# Revit family: IS_ConnectSpace_E1332_BIM_FR
name_source: partatom
category: Plumbing Fixtures
revit_build: Autodesk Revit 2017 (Build: 20160225_1515(x64)
units: mm (PartAtom-declared; Revit-internal decimal feet)

## family parameters
Always vertical = No
Cut with Voids When Loaded = No
OmniClass Number = 23.45.05.14.14
OmniClass Title = Sinks/Lavatories
Part Type = Normal
Room Calculation Point = No
Round Connector Dimension = Use Diameter
Shared = No
Work Plane-Based = No

## types (1)
- E1332 - Lavabo 55 x 38 cm
    Accessoires = www.idealstandard.be
    Assembly Code = C1030200
    Auteur = Ideal Standard
    BOSUseNativeGeometries = 1
    Caractéristiques = Lavabo 55 x 38 cm
    CodeBarre = 5017830447665
    ConseilsDInstallation = www.idealstandard.be
    Couleur = blanc
    CoûtDeRemplacement = 0
    DateDeCréation = 2018_08_15
    Description = Lavabo 55 x 38 cm
    Dimensions = 172 x 550 x 380
    DuréeDeGarantieDesPièces = 2
    DuréeGarantie = year
    DébitL/Mn = Litres
    DétailGarantie = Manufacturers Warranty
    Espace = Internal
    Finition = blanc
    Forme = Sculptured
    Hauteur = 172 mm
    IfcExportAs = IfcSanitaryType
    IfcExportType = WASHHANDBASIN
    InformationsProduit = www.idealstandard.be
    Largeur = 550 mm
    LienUtile = www.idealstandard.be
    Longueur = 380 mm
    Manufacturer = www.idealstandard.be
    Marque = Ideal Standard
    Matériel = Vitreous china
    Model = E1332
    Nom = Lavabo 55 x 38 cm
    PoidsBrut = 14
    PoidsNet = 14
    Révision = 1
    TypeDeLavabo = Washbasins
    URL = www.idealstandard.be
    UrlDuFabricant = www.idealstandard.be

## geometry (parser evidence)
native form markers: Sweep x3
no freeform markers — native parametric forms only
